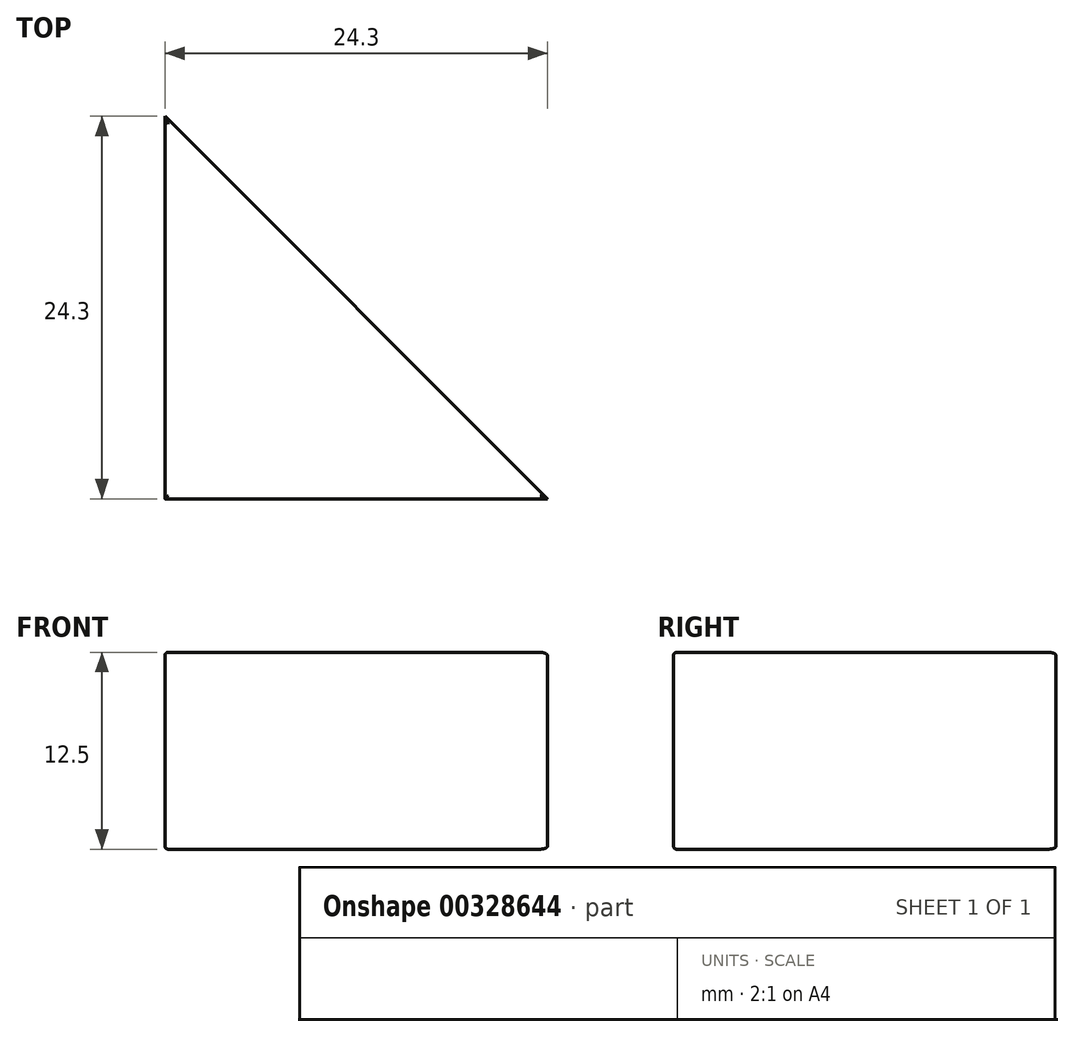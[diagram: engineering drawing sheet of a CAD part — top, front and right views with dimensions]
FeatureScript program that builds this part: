
annotation { "Feature Type Name" : "Feature", "Feature Type Description" : "" }
export const myFeature = defineFeature(function(context is Context, id is Id, definition is map)
    precondition{}
    {
        {
            var Q0;
            Q0=qCreatedBy(makeId("Top.planeOp"),FACE);
            var sketch = newSketch(context, id + "F0", { "sketchPlane" : qUnion([Q0])});
            skLineSegment(sketch, "E0.bottom", {"start": v(0, 0) * mm, "end": v(24.3, 0) * mm});
            skLineSegment(sketch, "E0.left", {"start": v(0, 0) * mm, "end": v(0, 24.3) * mm});
            skLineSegment(sketch, "E1", {"start": v(0, 24.3) * mm, "end": v(24.3, 0) * mm});
            skSolve(sketch);
        }
        {
            var Q0;
            Q0=qSketchRegion(id+"F0",true);
            extrude(context, id + "F1", {"entities" : qUnion([Q0]), "oppositeDirection" : true, "depth" : 12.5 * mm});
        }
        {
            var Q0;
            Q0=makeQuery(id+"F1.opExtrude","CAP_FACE",FACE,{"disambiguationData":[OSD([sQuery(id+"F0.wireOp",EDGE,"E0.bottom"),sQuery(id+"F0.wireOp",EDGE,"E0.top"),sQuery(id+"F0.wireOp",EDGE,"E0.left"),sQuery(id+"F0.wireOp",EDGE,"E0.right")])],"isStart":true});
            var Q1;
            Q1=makeQuery(id+"F1.opExtrude","CAP_FACE",FACE,{"disambiguationData":[OSD([sQuery(id+"F0.wireOp",EDGE,"E0.bottom"),sQuery(id+"F0.wireOp",EDGE,"E0.top"),sQuery(id+"F0.wireOp",EDGE,"E0.left"),sQuery(id+"F0.wireOp",EDGE,"E0.right")])],"isStart":false});
            fillet(context, id + "F2", {"entities" : qUnion([Q0, Q1]), "radius" : .2 * mm, "tangentPropagation" : true, "allowEdgeOverflow" : false});
        }
    });
